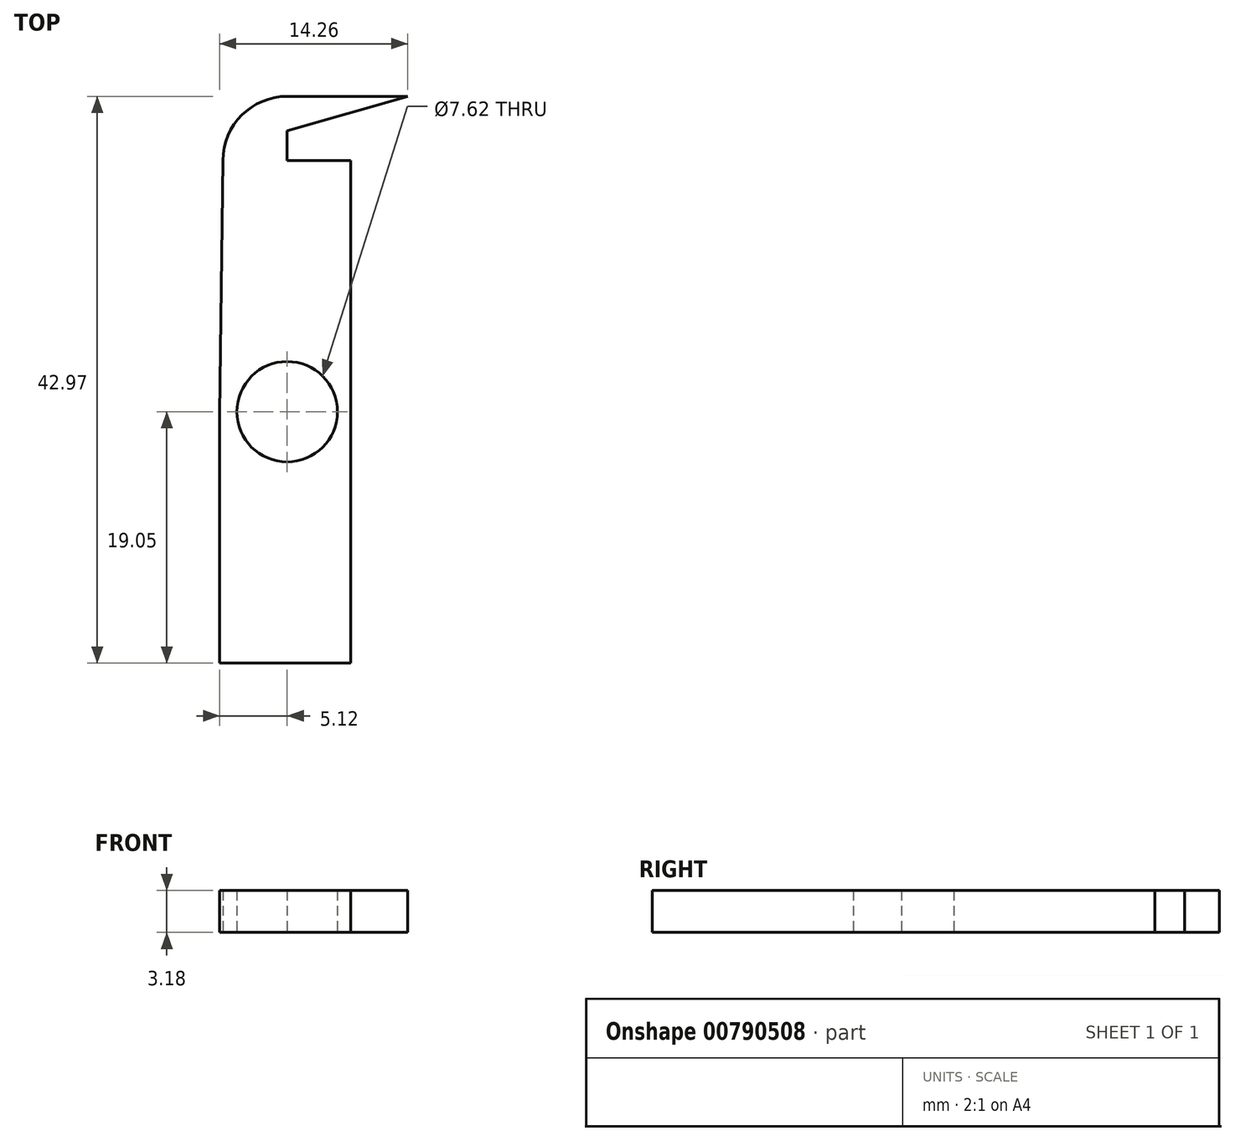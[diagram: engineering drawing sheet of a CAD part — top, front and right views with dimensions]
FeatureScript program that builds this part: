
annotation { "Feature Type Name" : "Feature", "Feature Type Description" : "" }
export const myFeature = defineFeature(function(context is Context, id is Id, definition is map)
    precondition{}
    {
        {
            var Q0;
            Q0=qCreatedBy(makeId("Top.planeOp"),FACE);
            var sketch = newSketch(context, id + "F0", { "sketchPlane" : qUnion([Q0])});
            skLineSegment(sketch, "E0", {"start": v(0, 0) * mm, "end": v(0, 38.1) * mm});
            skLineSegment(sketch, "E1", {"start": v(0, 0) * mm, "end": v(4.83, 0) * mm});
            skLineSegment(sketch, "E2", {"start": v(0, 0) * mm, "end": v(-5.12, 0) * mm});
            skLineSegment(sketch, "E3", {"start": v(-5.12, 0) * mm, "end": v(-5.12, 37.75) * mm});
            skLineSegment(sketch, "E4", {"start": v(4.83, 4.83) * mm, "end": v(4.83, 0) * mm});
            skLineSegment(sketch, "E5", {"start": v(4.83, 38.1) * mm, "end": v(4.83, 4.83) * mm});
            skCircle(sketch, "E6", {"center": v(0, 18.87) * mm, "radius": 4.83 * mm});
            skPoint(sketch, "E6.centerSnap0", {"position": v(0, 19.05) * mm});
            skPoint(sketch, "E6.centerSnap1", {"position": v(-5.12, 18.87) * mm});
            skArc(sketch, "E7", {"start": v(0, 42.97) * mm, "mid": v(-3.44, 41.54) * mm, "end": v(-4.87, 38.1) * mm});
            skLineSegment(sketch, "E8", {"start": v(0, 42.97) * mm, "end": v(9.14, 42.97) * mm});
            skLineSegment(sketch, "E9", {"start": v(9.14, 42.97) * mm, "end": v(0, 40.36) * mm});
            skLineSegment(sketch, "E10", {"start": v(0, 40.36) * mm, "end": v(0, 38.1) * mm});
            skLineSegment(sketch, "E11", {"start": v(4.83, 38.1) * mm, "end": v(0, 38.1) * mm});
            skLineSegment(sketch, "E12", {"start": v(0, 19.05) * mm, "end": v(0, 0) * mm});
            skLineSegment(sketch, "E13", {"start": v(-5.12, 18.87) * mm, "end": v(-5.12, 0) * mm});
            skLineSegment(sketch, "E14", {"start": v(-5.12, 18.87) * mm, "end": v(-4.87, 38.1) * mm});
            skLineSegment(sketch, "E15", {"start": v(4.83, 0) * mm, "end": v(-5.12, 0) * mm});
            skSolve(sketch);
        }
        {
            var Q0;
            Q0=makeQuery(id+"F0.imprint","IMPRINT",FACE,{"disambiguationData":[TD([[makeQuery(id+"F0.imprint","IMPRINT",EDGE,{"derivedFrom":sQuery(id+"F0.wireOp",EDGE,"E7")}),1.0]])]});
            var Q1;
            {var subQ0=sQuery(id+"F0.wireOp",EDGE,"E11");Q1=makeQuery(id+"F0.imprint","IMPRINT",FACE,{"disambiguationData":[TD([[makeQuery(id+"F0.imprint","IMPRINT",EDGE,{"derivedFrom":subQ0}),1.0]])]});}
            var Q2;
            {var subQ0=sQuery(id+"F0.wireOp",EDGE,"E12");var subQ1=sQuery(id+"F0.wireOp",EDGE,"E0");var subQ2=makeQuery(id+"F0.imprint","INTERSECT",VERTEX,{"derivedFrom":[subQ1,subQ0]});Q2=makeQuery(id+"F0.imprint","IMPRINT",FACE,{"disambiguationData":[TD([[makeQuery(id+"F0.imprint","IMPRINT",EDGE,{"disambiguationData":[TD([[subQ2,-1.0]])],"derivedFrom":subQ1}),-1.0]])]});}
            var Q3;
            {var subQ0=sQuery(id+"F0.wireOp",EDGE,"E12");var subQ1=sQuery(id+"F0.wireOp",EDGE,"E0");var subQ2=makeQuery(id+"F0.imprint","INTERSECT",VERTEX,{"derivedFrom":[subQ1,subQ0]});Q3=makeQuery(id+"F0.imprint","IMPRINT",FACE,{"disambiguationData":[TD([[makeQuery(id+"F0.imprint","IMPRINT",EDGE,{"disambiguationData":[TD([[subQ2,-1.0]])],"derivedFrom":subQ1}),1.0]])]});}
            var Q4;
            {var subQ5=sQuery(id+"F0.wireOp",EDGE,"E4");Q4=makeQuery(id+"F0.imprint","IMPRINT",FACE,{"disambiguationData":[TD([[makeQuery(id+"F0.imprint","IMPRINT",EDGE,{"derivedFrom":subQ5}),-1.0]])]});}
            extrude(context, id + "F1", {"entities" : qUnion([Q0, Q1, Q2, Q3, Q4]), "depth" : 3.17 * mm, "offsetDistance" : 25.4 * mm});
        }
        {
            var Q0;
            Q0 = qSketchRegion(id + "F0", true);
            var Q1;
            Q1=makeQuery(id+"F1.opExtrude","CAP_FACE",FACE,{"disambiguationData":[OSD([sQuery(id+"F0.wireOp",EDGE,"E4"),sQuery(id+"F0.wireOp",EDGE,"E7"),sQuery(id+"F0.wireOp",EDGE,"E8"),sQuery(id+"F0.wireOp",EDGE,"E9"),sQuery(id+"F0.wireOp",EDGE,"E10"),sQuery(id+"F0.wireOp",EDGE,"E11"),sQuery(id+"F0.wireOp",EDGE,"E5"),sQuery(id+"F0.wireOp",EDGE,"E13"),sQuery(id+"F0.wireOp",EDGE,"E14"),sQuery(id+"F0.wireOp",EDGE,"E15")])],"isStart":true});
            extrude(context, id + "F2", {"entities" : qUnion([Q0, Q1]), "operationType" : NewBodyOperationType.REMOVE, "oppositeDirection" : true, "depth" : 25.4 * mm, "offsetDistance" : 25.4 * mm});
        }
        {
            var Q0;
            Q0=sQuery(id+"F0.wireOp",VERTEX,"E6.centerSnap0");
            var Q1;
            Q1=makeQuery(id+"F1.opExtrude","SWEPT_BODY",BODY,{"disambiguationData":[OSD([sQuery(id+"F0.wireOp",EDGE,"E4"),sQuery(id+"F0.wireOp",EDGE,"E7"),sQuery(id+"F0.wireOp",EDGE,"E8"),sQuery(id+"F0.wireOp",EDGE,"E9"),sQuery(id+"F0.wireOp",EDGE,"E10"),sQuery(id+"F0.wireOp",EDGE,"E11"),sQuery(id+"F0.wireOp",EDGE,"E5"),sQuery(id+"F0.wireOp",EDGE,"E13"),sQuery(id+"F0.wireOp",EDGE,"E14"),sQuery(id+"F0.wireOp",EDGE,"E15")])]});
            hole(context, id + "F3", {"style" : HoleStyle.SIMPLE, "endStyle" : HoleEndStyle.THROUGH, "oppositeDirection" : true, "holeDiameter" : 7.62 * mm, "majorDiameter" : 6.35 * mm, "isTappedThrough" : true, "tappedDepth" : 12.7 * mm, "tapClearance" : 3, "locations" : qUnion([Q0]), "scope" : qUnion([Q1])});
        }
    });
